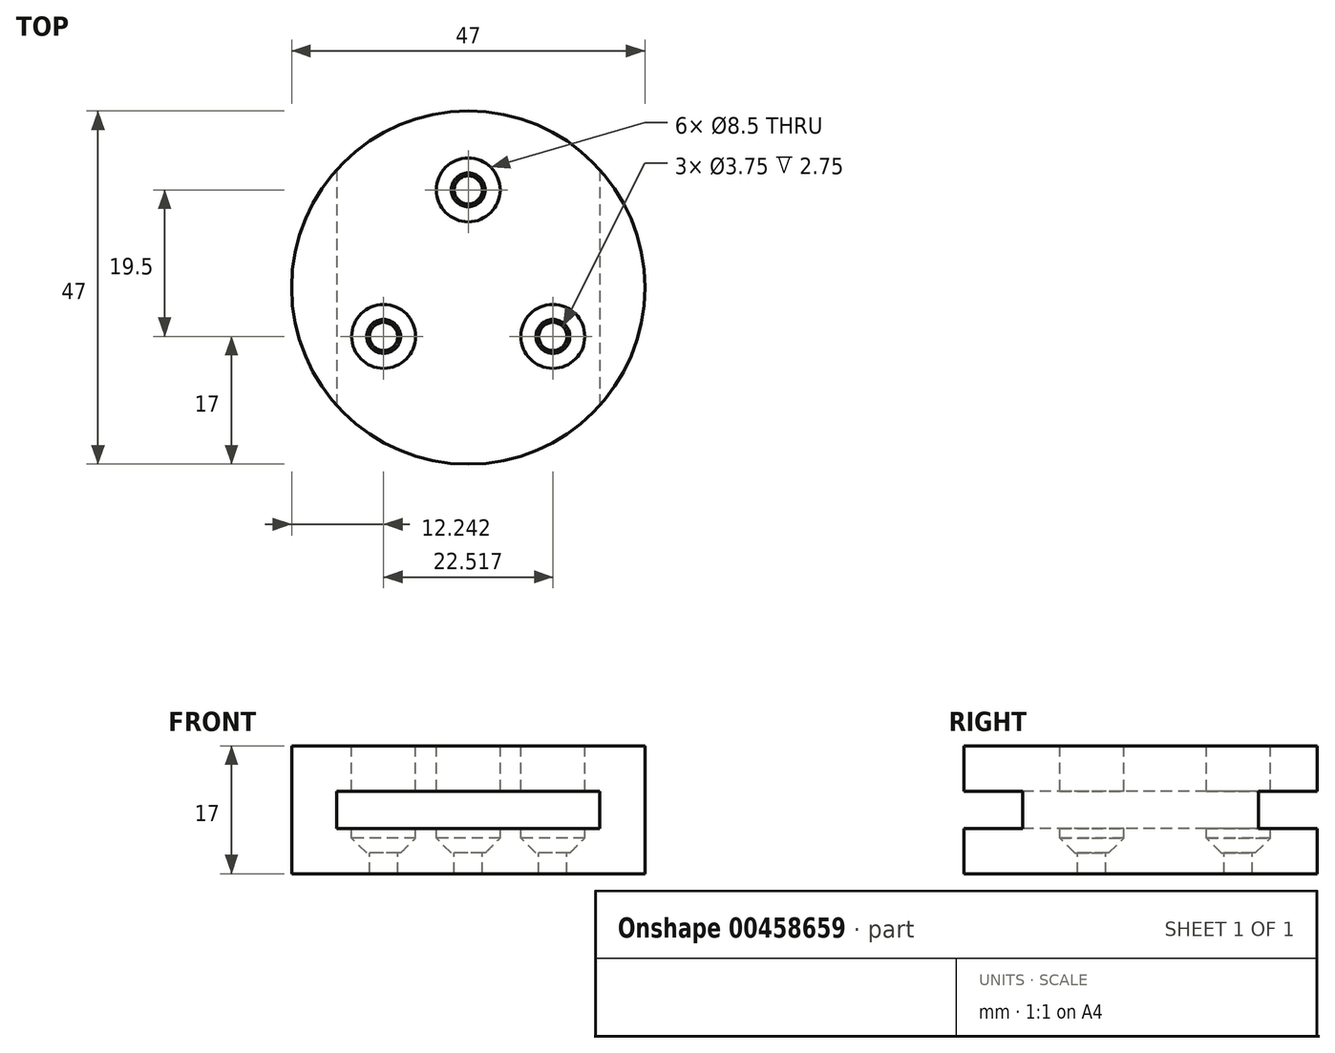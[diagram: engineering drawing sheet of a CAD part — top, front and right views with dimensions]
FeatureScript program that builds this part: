
annotation { "Feature Type Name" : "Feature", "Feature Type Description" : "" }
export const myFeature = defineFeature(function(context is Context, id is Id, definition is map)
    precondition{}
    {
        {
            var Q0;
            Q0=qCreatedBy(makeId("Top.planeOp"),FACE);
            var sketch = newSketch(context, id + "F0", { "sketchPlane" : qUnion([Q0])});
            skCircle(sketch, "E0", {"center": v(0, 0) * mm, "radius": 23.5 * mm});
            skSolve(sketch);
        }
        {
            var Q0;
            Q0=makeQuery(id+"F0.imprint","IMPRINT",FACE,{"disambiguationData":[TD([[makeQuery(id+"F0.imprint","IMPRINT",EDGE,{"derivedFrom":sQuery(id+"F0.wireOp",EDGE,"E0")}),1.0]])]});
            extrude(context, id + "F1", {"entities" : qUnion([Q0]), "depth" : 17 * mm});
        }
        {
            var Q0;
            Q0=qCreatedBy(makeId("Front.planeOp"),FACE);
            var sketch = newSketch(context, id + "F2", { "sketchPlane" : qUnion([Q0])});
            skLineSegment(sketch, "E1.bottom", {"start": v(17.5, 11) * mm, "end": v(-17.5, 11) * mm});
            skLineSegment(sketch, "E1.top", {"start": v(17.5, 6) * mm, "end": v(-17.5, 6) * mm});
            skLineSegment(sketch, "E1.left", {"start": v(17.5, 11) * mm, "end": v(17.5, 6) * mm});
            skLineSegment(sketch, "E1.right", {"start": v(-17.5, 11) * mm, "end": v(-17.5, 6) * mm});
            skPoint(sketch, "E1.middle", {"position": v(0, 8.5) * mm});
            skSolve(sketch);
        }
        {
            var Q0;
            Q0 = qSketchRegion(id + "F2", true);
            extrude(context, id + "F3", {"entities" : qUnion([Q0]), "operationType" : NewBodyOperationType.REMOVE, "endBound" : BoundingType.SYMMETRIC, "oppositeDirection" : true, "depth" : 57.2 * mm});
        }
        {
            var Q0;
            Q0=makeQuery(id+"F1.opExtrude","CAP_FACE",FACE,{"disambiguationData":[OSD([sQuery(id+"F0.wireOp",EDGE,"E0")])],"isStart":false});
            var sketch = newSketch(context, id + "F4", { "sketchPlane" : qUnion([Q0])});
            skCircle(sketch, "E2", {"center": v(0, 13) * mm, "radius": 1.88 * mm});
            skCircle(sketch, "E3.1.0", {"center": v(-11.26, -6.5) * mm, "radius": 1.88 * mm});
            skCircle(sketch, "E3.2.0", {"center": v(11.26, -6.5) * mm, "radius": 1.88 * mm});
            skPoint(sketch, "E3.center", {"position": v(0, 0) * mm});
            skSolve(sketch);
        }
        {
            var Q0;
            Q0 = qSketchRegion(id + "F4", true);
            extrude(context, id + "F5", {"entities" : qUnion([Q0]), "operationType" : NewBodyOperationType.REMOVE, "endBound" : BoundingType.THROUGH_ALL, "oppositeDirection" : true, "depth" : 25 * mm});
        }
        {
            var Q0;
            Q0=makeQuery(id+"F1.opExtrude","CAP_FACE",FACE,{"disambiguationData":[OSD([sQuery(id+"F0.wireOp",EDGE,"E0")])],"isStart":false});
            var sketch = newSketch(context, id + "F6", { "sketchPlane" : qUnion([Q0])});
            skCircle(sketch, "E4", {"center": v(0, 13) * mm, "radius": 4.25 * mm});
            skCircle(sketch, "E5.1.0", {"center": v(-11.26, -6.5) * mm, "radius": 4.25 * mm});
            skCircle(sketch, "E5.2.0", {"center": v(11.26, -6.5) * mm, "radius": 4.25 * mm});
            skPoint(sketch, "E5.center", {"position": v(0, 0) * mm});
            skSolve(sketch);
        }
        {
            var Q0;
            Q0 = qSketchRegion(id + "F6", true);
            extrude(context, id + "F7", {"entities" : qUnion([Q0]), "operationType" : NewBodyOperationType.REMOVE, "oppositeDirection" : true, "depth" : 14.25 * mm});
        }
        {
            var Q0;
            Q0=makeQuery(id+"F7.boolean.opBoolean","COPY",EDGE,{"derivedFrom":makeQuery(id+"F7.opExtrude","CAP_EDGE",EDGE,{"disambiguationData":[OSD([sQuery(id+"F6.wireOp",EDGE,"E5.1.0")])],"isStart":false})});
            var Q1;
            Q1=makeQuery(id+"F7.boolean.opBoolean","COPY",EDGE,{"derivedFrom":makeQuery(id+"F7.opExtrude","CAP_EDGE",EDGE,{"disambiguationData":[OSD([sQuery(id+"F6.wireOp",EDGE,"E5.2.0")])],"isStart":false})});
            var Q2;
            Q2=makeQuery(id+"F7.boolean.opBoolean","COPY",EDGE,{"derivedFrom":makeQuery(id+"F7.opExtrude","CAP_EDGE",EDGE,{"disambiguationData":[OSD([sQuery(id+"F6.wireOp",EDGE,"E4")])],"isStart":false})});
            chamfer(context, id + "F8", {"entities" : qUnion([Q0, Q1, Q2]), "width" : 2 * mm, "tangentPropagation" : true});
        }
    });
